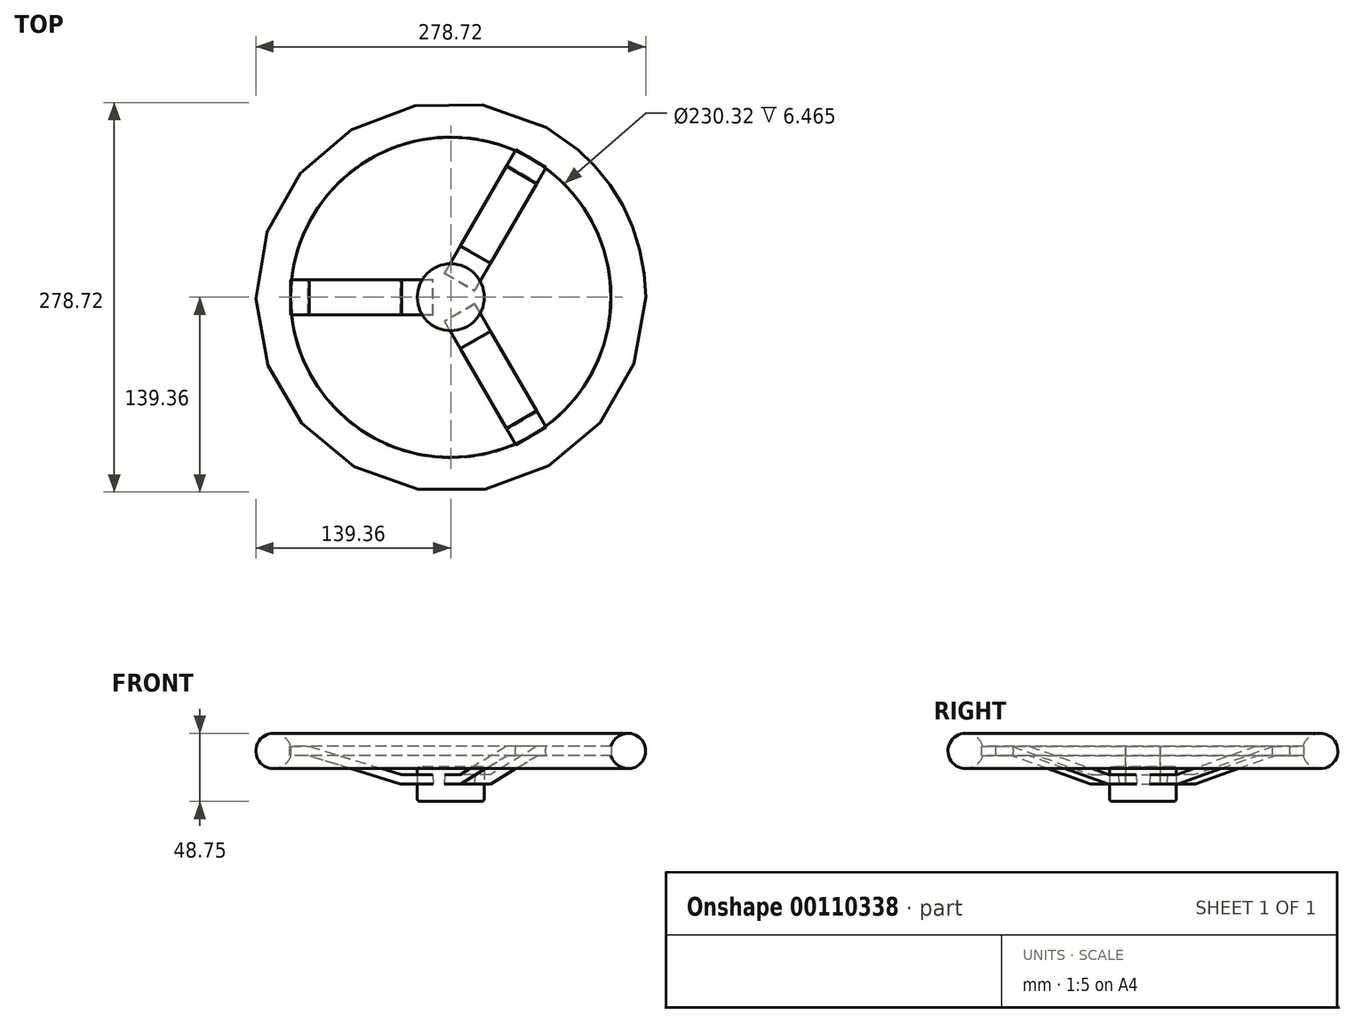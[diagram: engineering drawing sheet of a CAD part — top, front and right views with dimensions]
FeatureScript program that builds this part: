
annotation { "Feature Type Name" : "Feature", "Feature Type Description" : "" }
export const myFeature = defineFeature(function(context is Context, id is Id, definition is map)
    precondition{}
    {
        {
            var Q0;
            Q0=qCreatedBy(makeId("Front.planeOp"),FACE);
            var sketch = newSketch(context, id + "F0", { "sketchPlane" : qUnion([Q0])});
            skLineSegment(sketch, "E0", {"start": v(-12.53, 0) * mm, "end": v(-35.96, 0) * mm});
            skLineSegment(sketch, "E1", {"start": v(-35.96, 0) * mm, "end": v(-102.23, 20.4) * mm});
            skLineSegment(sketch, "E2", {"start": v(-102.23, 20.4) * mm, "end": v(-115.16, 20.4) * mm});
            skLineSegment(sketch, "E3", {"start": v(-115.16, 20.4) * mm, "end": v(-115.16, 26.87) * mm});
            skLineSegment(sketch, "E4", {"start": v(-115.16, 26.87) * mm, "end": v(-101.02, 26.87) * mm});
            skLineSegment(sketch, "E5", {"start": v(-101.02, 26.87) * mm, "end": v(-35.18, 6.6) * mm});
            skLineSegment(sketch, "E6", {"start": v(-35.18, 6.6) * mm, "end": v(-12.93, 6.6) * mm});
            skLineSegment(sketch, "E7", {"start": v(-12.93, 6.6) * mm, "end": v(-12.53, 0) * mm});
            skLineSegment(sketch, "E8", {"start": v(0, 48.28) * mm, "end": v(0, -49.13) * mm, "construction": true});
            skCircle(sketch, "E9", {"center": v(-126.73, 23.62) * mm, "radius": 12.64 * mm});
            skSolve(sketch);
        }
        {
            var Q0;
            Q0=makeQuery(id+"F0.imprint","IMPRINT",FACE,{"disambiguationData":[TD([[makeQuery(id+"F0.imprint","IMPRINT",EDGE,{"derivedFrom":sQuery(id+"F0.wireOp",EDGE,"E0")}),-1.0]])]});
            extrude(context, id + "F1", {"entities" : qUnion([Q0]), "endBound" : BoundingType.SYMMETRIC, "depth" : 25 * mm});
        }
        {
            var Q0;
            Q0=makeQuery(id+"F1.opExtrude","SWEPT_BODY",BODY,{"disambiguationData":[OSD([sQuery(id+"F0.wireOp",EDGE,"E0"),sQuery(id+"F0.wireOp",EDGE,"E1"),sQuery(id+"F0.wireOp",EDGE,"E2"),sQuery(id+"F0.wireOp",EDGE,"E3"),sQuery(id+"F0.wireOp",EDGE,"E4"),sQuery(id+"F0.wireOp",EDGE,"E5"),sQuery(id+"F0.wireOp",EDGE,"E6"),sQuery(id+"F0.wireOp",EDGE,"E7")])]});
            var Q1;
            Q1=sQuery(id+"F0.wireOp",EDGE,"E8");
            circularPattern(context, id + "F2", {"entities" : qUnion([Q0]), "axis" : qUnion([Q1]), "angle" : 120 * degree, "instanceCount" : 3});
        }
        {
            var Q0;
            {var subQ0=sQuery(id+"F0.wireOp",EDGE,"E3");Q0=makeQuery(id+"F0.imprint","IMPRINT",FACE,{"disambiguationData":[TD([[makeQuery(id+"F0.imprint","IMPRINT",EDGE,{"derivedFrom":subQ0}),1.0]])]});}
            var Q1;
            Q1=sQuery(id+"F0.wireOp",EDGE,"E8");
            revolve(context, id + "F3", {"entities" : qUnion([Q0]), "axis" : qUnion([Q1]), "revolveType" : RevolveType.FULL});
        }
        {
            var Q0;
            Q0=qCreatedBy(makeId("Top.planeOp"),FACE);
            var sketch = newSketch(context, id + "F4", { "sketchPlane" : qUnion([Q0])});
            skCircle(sketch, "E10", {"center": v(0, 0) * mm, "radius": 23.94 * mm});
            skSolve(sketch);
        }
        {
            var Q0;
            Q0=makeQuery(id+"F4.imprint","IMPRINT",FACE,{"disambiguationData":[TD([[makeQuery(id+"F4.imprint","IMPRINT",EDGE,{"derivedFrom":sQuery(id+"F4.wireOp",EDGE,"E10")}),1.0]])]});
            extrude(context, id + "F5", {"entities" : qUnion([Q0]), "endBound" : BoundingType.SYMMETRIC, "depth" : 25 * mm});
        }
        {
            var Q0;
            Q0=makeQuery(id+"F5.opExtrude","CAP_EDGE",EDGE,{"disambiguationData":[OSD([sQuery(id+"F4.wireOp",EDGE,"E10")])],"isStart":false});
            var Q1;
            Q1=makeQuery(id+"F5.opExtrude","CAP_EDGE",EDGE,{"disambiguationData":[OSD([sQuery(id+"F4.wireOp",EDGE,"E10")])],"isStart":true});
            fillet(context, id + "F6", {"entities" : qUnion([Q0, Q1]), "radius" : 2 * mm, "tangentPropagation" : true, "allowEdgeOverflow" : false});
        }
    });
